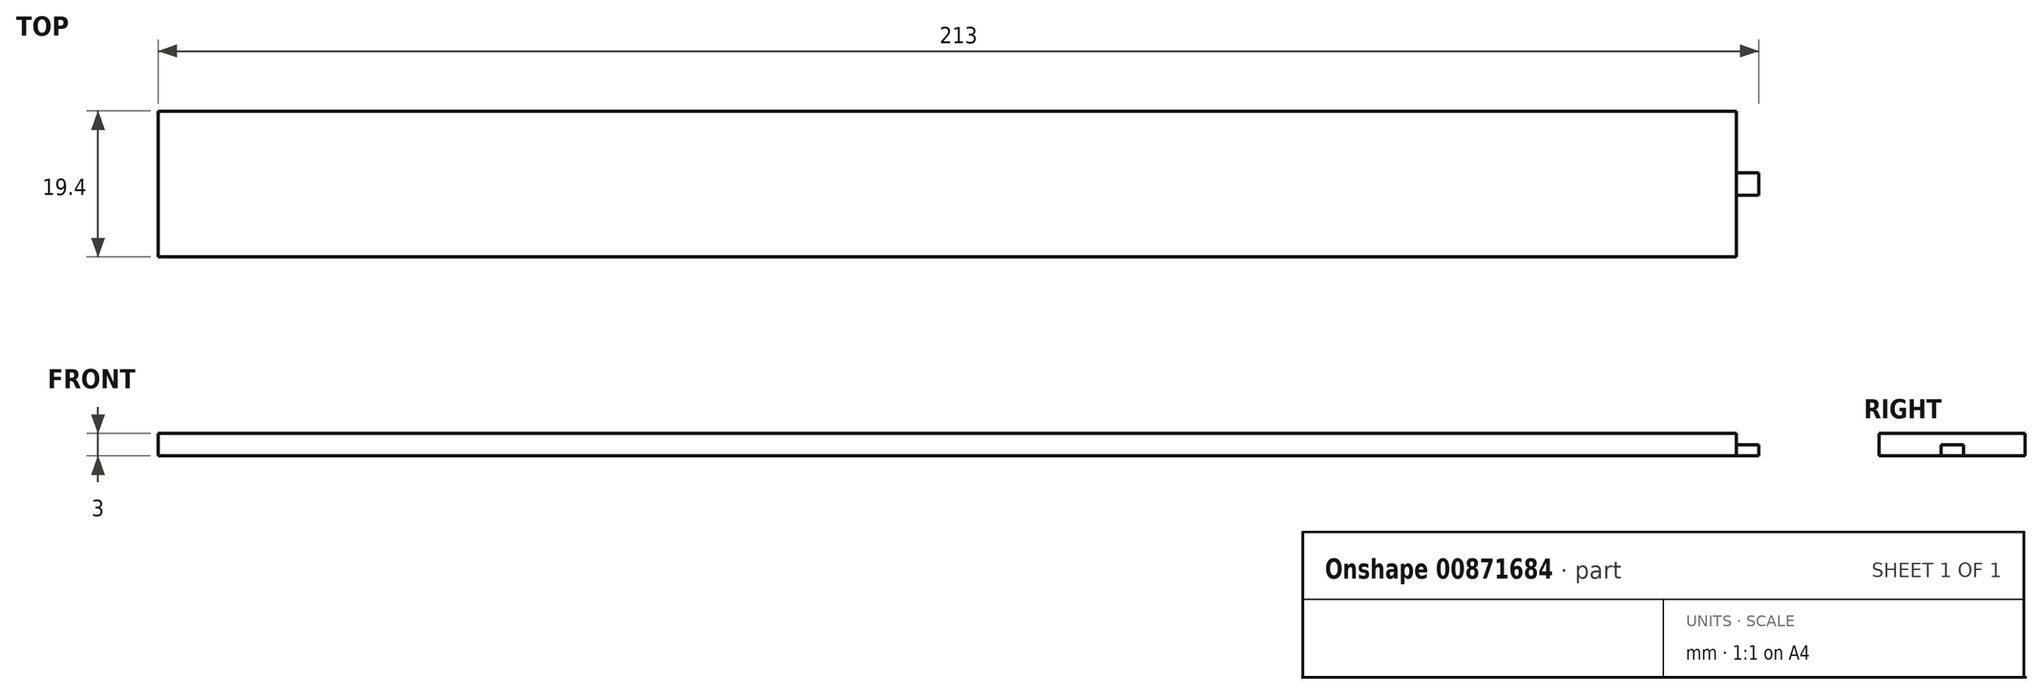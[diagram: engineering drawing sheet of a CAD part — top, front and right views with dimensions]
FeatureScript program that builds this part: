
annotation { "Feature Type Name" : "Feature", "Feature Type Description" : "" }
export const myFeature = defineFeature(function(context is Context, id is Id, definition is map)
    precondition{}
    {
        {
            var Q0;
            Q0=qCreatedBy(makeId("Top.planeOp"),FACE);
            var sketch = newSketch(context, id + "F0", { "sketchPlane" : qUnion([Q0])});
            skLineSegment(sketch, "E0.bottom", {"start": v(105, -9.7) * mm, "end": v(-105, -9.7) * mm});
            skLineSegment(sketch, "E0.top", {"start": v(105, 9.7) * mm, "end": v(-105, 9.7) * mm});
            skLineSegment(sketch, "E0.left", {"start": v(105, -9.7) * mm, "end": v(105, 9.7) * mm});
            skLineSegment(sketch, "E0.right", {"start": v(-105, -9.7) * mm, "end": v(-105, 9.7) * mm});
            skPoint(sketch, "E0.middle", {"position": v(0, 0) * mm});
            skSolve(sketch);
        }
        {
            var Q0;
            Q0 = qSketchRegion(id + "F0", true);
            extrude(context, id + "F1", {"entities" : qUnion([Q0]), "depth" : 3 * mm, "offsetDistance" : 25 * mm});
        }
        {
            var Q0;
            Q0=makeQuery(id+"F1.opExtrude","SWEPT_FACE",FACE,{"disambiguationData":[OSD([sQuery(id+"F0.wireOp",EDGE,"E0.left")])]});
            var sketch = newSketch(context, id + "F2", { "sketchPlane" : qUnion([Q0])});
            skLineSegment(sketch, "E1.bottom", {"start": v(-1.5, 1.5) * mm, "end": v(1.5, 1.5) * mm});
            skLineSegment(sketch, "E1.top", {"start": v(-1.5, 0) * mm, "end": v(1.5, 0) * mm});
            skLineSegment(sketch, "E1.left", {"start": v(-1.5, 1.5) * mm, "end": v(-1.5, 0) * mm});
            skLineSegment(sketch, "E1.right", {"start": v(1.5, 1.5) * mm, "end": v(1.5, 0) * mm});
            skLineSegment(sketch, "E2", {"start": v(0, 0) * mm, "end": v(0, 1.96) * mm, "construction": true});
            skSolve(sketch);
        }
        {
            var Q0;
            Q0 = qSketchRegion(id + "F2", true);
            extrude(context, id + "F3", {"entities" : qUnion([Q0]), "operationType" : NewBodyOperationType.ADD, "depth" : 3 * mm, "offsetDistance" : 25 * mm});
        }
    });
